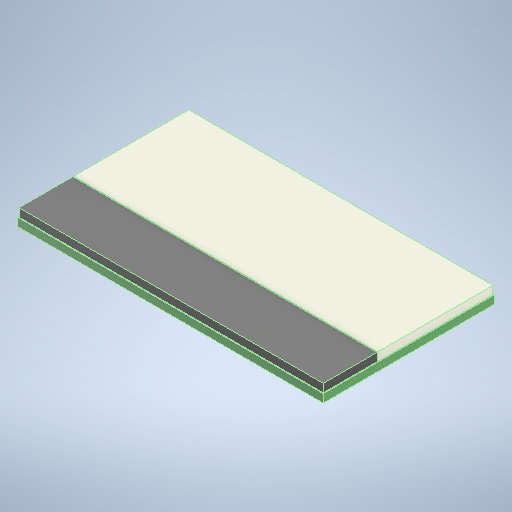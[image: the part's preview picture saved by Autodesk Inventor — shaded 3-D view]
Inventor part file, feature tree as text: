
AUTODESK INVENTOR PART (.ipt)
format: ipt  version: 2025.3 (Build 293356000, 356)  size: 250,368 bytes
history: native  units: mm
features: extrude x3, sketch x3, other x1
ambient origin geometry x8: Origin, YZ Plane, XZ Plane, XY Plane, X Axis, Y Axis, Z Axis, Center Point
bodies: Body1 (feature_tree)
feature tree (7):
  other  "ソリッド1"
  extrude  "押し出し1"  Depth=41.2mm
  extrude  "押し出し2"  Depth=23.07mm
  extrude  "押し出し3"  Depth=1.1mm TaperAngle=0.0deg
  sketch  "スケッチ1"
  sketch  "スケッチ3"
  sketch  "スケッチ4"
